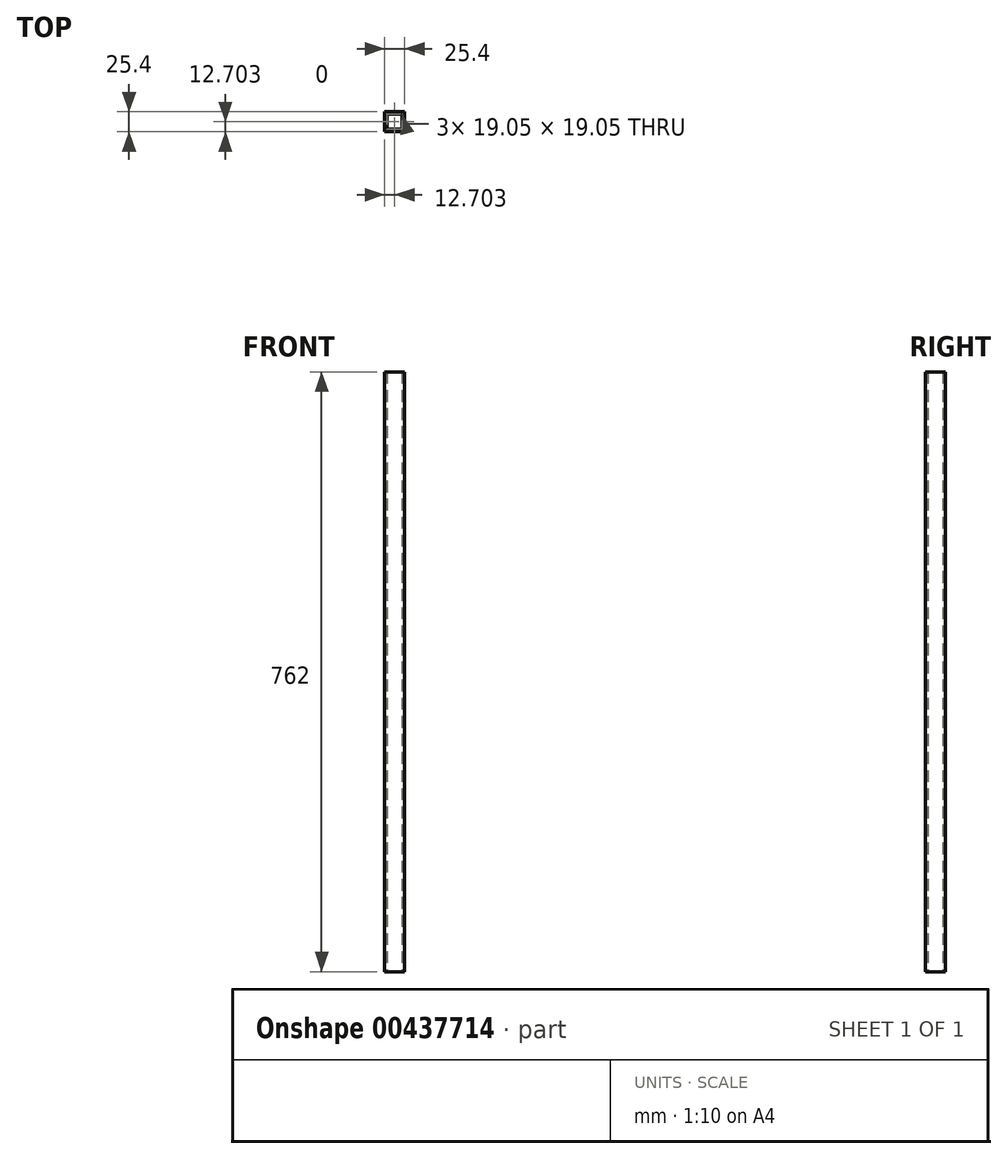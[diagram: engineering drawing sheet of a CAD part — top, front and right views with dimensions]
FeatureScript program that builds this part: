
annotation { "Feature Type Name" : "Feature", "Feature Type Description" : "" }
export const myFeature = defineFeature(function(context is Context, id is Id, definition is map)
    precondition{}
    {
        {
            var Q0;
            Q0=qCreatedBy(makeId("Top.planeOp"),FACE);
            var sketch = newSketch(context, id + "F0", { "sketchPlane" : qUnion([Q0])});
            skLineSegment(sketch, "E0.bottom", {"start": v(-39.15, 47.4) * mm, "end": v(-13.75, 47.4) * mm});
            skLineSegment(sketch, "E0.top", {"start": v(-39.15, 22) * mm, "end": v(-13.75, 22) * mm});
            skLineSegment(sketch, "E0.left", {"start": v(-39.15, 47.4) * mm, "end": v(-39.15, 22) * mm});
            skLineSegment(sketch, "E0.right", {"start": v(-13.75, 47.4) * mm, "end": v(-13.75, 22) * mm});
            skSolve(sketch);
        }
        {
            var Q0;
            Q0 = qSketchRegion(id + "F0", true);
            extrude(context, id + "F1", {"entities" : qUnion([Q0]), "depth" : 762 * mm});
        }
        {
            var Q0;
            Q0=makeQuery(id+"F1.opExtrude","CAP_FACE",FACE,{"disambiguationData":[OSD([sQuery(id+"F0.wireOp",EDGE,"E0.bottom"),sQuery(id+"F0.wireOp",EDGE,"E0.top"),sQuery(id+"F0.wireOp",EDGE,"E0.left"),sQuery(id+"F0.wireOp",EDGE,"E0.right")])],"isStart":true});
            var sketch = newSketch(context, id + "F2", { "sketchPlane" : qUnion([Q0])});
            skLineSegment(sketch, "E1.bottom", {"start": v(-35.97, -25.18) * mm, "end": v(-16.92, -25.18) * mm});
            skLineSegment(sketch, "E1.top", {"start": v(-35.97, -44.23) * mm, "end": v(-16.92, -44.23) * mm});
            skLineSegment(sketch, "E1.left", {"start": v(-35.97, -25.18) * mm, "end": v(-35.97, -44.23) * mm});
            skLineSegment(sketch, "E1.right", {"start": v(-16.92, -25.18) * mm, "end": v(-16.92, -44.23) * mm});
            skSolve(sketch);
        }
        {
            var Q0;
            Q0=makeQuery(id+"F2.imprint","IMPRINT",FACE,{"disambiguationData":[TD([[makeQuery(id+"F2.imprint","IMPRINT",EDGE,{"derivedFrom":sQuery(id+"F2.wireOp",EDGE,"E1.bottom")}),-1.0]])]});
            extrude(context, id + "F3", {"entities" : qUnion([Q0]), "operationType" : NewBodyOperationType.REMOVE, "oppositeDirection" : true, "depth" : 762 * mm});
        }
    });
